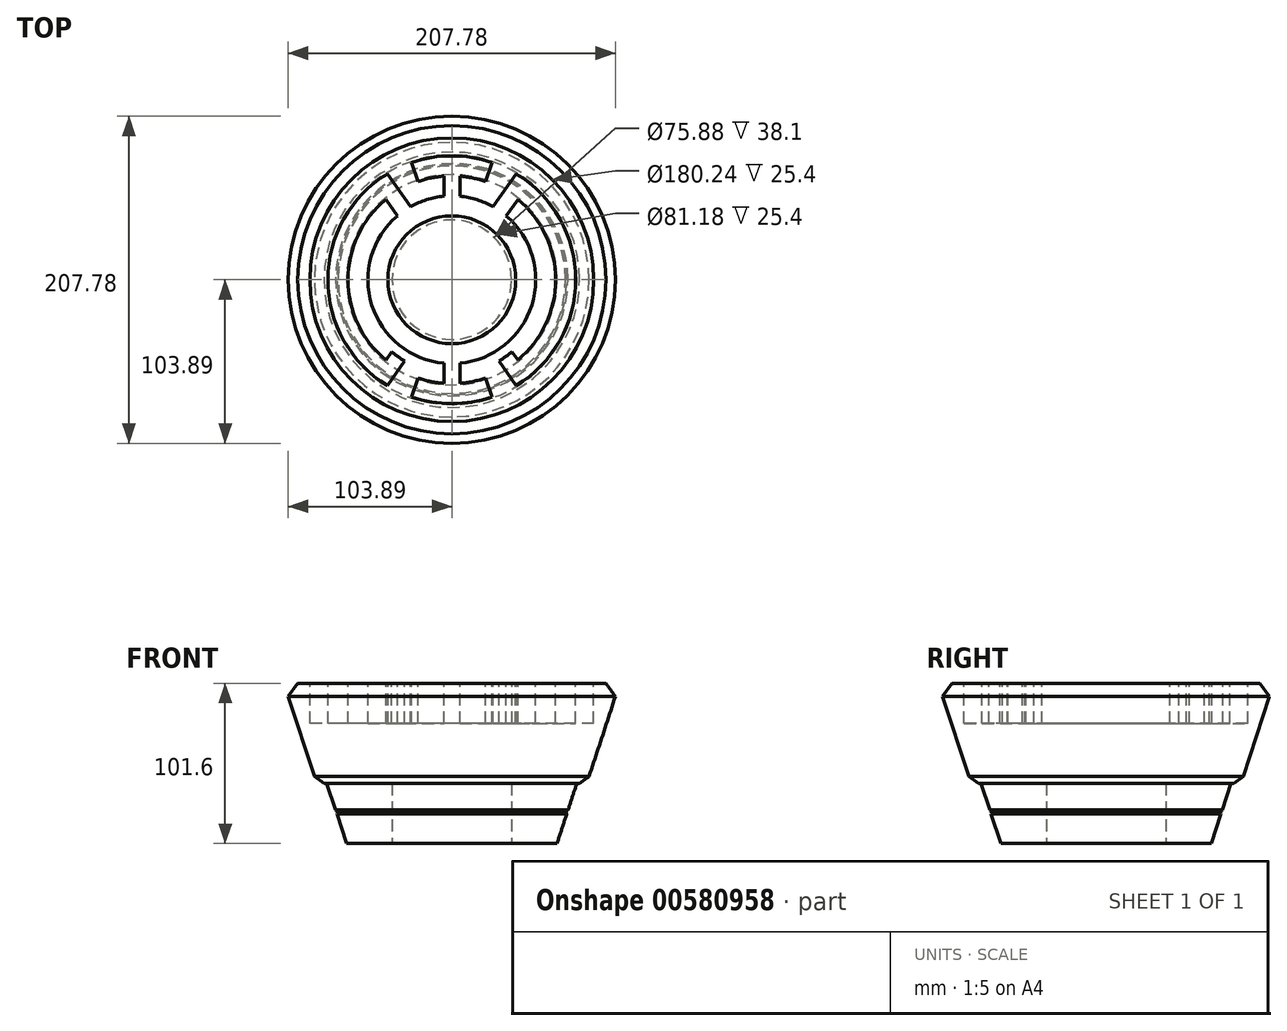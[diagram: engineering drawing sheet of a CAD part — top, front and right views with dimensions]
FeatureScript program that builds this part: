
annotation { "Feature Type Name" : "Feature", "Feature Type Description" : "" }
export const myFeature = defineFeature(function(context is Context, id is Id, definition is map)
    precondition{}
    {
        {
            var Q0;
            Q0=qCreatedBy(makeId("Top.planeOp"),FACE);
            var sketch = newSketch(context, id + "F0", { "sketchPlane" : qUnion([Q0])});
            skCircle(sketch, "E0", {"center": v(0, 0) * mm, "radius": 66.85 * mm});
            skSolve(sketch);
        }
        {
            var Q0;
            Q0=qCreatedBy(makeId("Top.planeOp"),FACE);
            cPlane(context, id + "F1", {"entities" : qUnion([Q0]), "cplaneType" : CPlaneType.OFFSET, "offset" : 101.6 * mm, "width" : 152.4 * mm, "height" : 152.4 * mm});
        }
        {
            var Q0;
            Q0=qCreatedBy(id+"F1.planeOp",FACE);
            var sketch = newSketch(context, id + "F2", { "sketchPlane" : qUnion([Q0])});
            skCircle(sketch, "E1", {"center": v(0, 0) * mm, "radius": 100.28 * mm});
            skSolve(sketch);
        }
        {
            var Q0;
            Q0=makeQuery(id+"F2.imprint","IMPRINT",FACE,{"disambiguationData":[TD([[makeQuery(id+"F2.imprint","IMPRINT",EDGE,{"derivedFrom":sQuery(id+"F2.wireOp",EDGE,"E1")}),1.0]])]});
            var Q1;
            Q1=makeQuery(id+"F0.imprint","IMPRINT",FACE,{"disambiguationData":[TD([[makeQuery(id+"F0.imprint","IMPRINT",EDGE,{"derivedFrom":sQuery(id+"F0.wireOp",EDGE,"E0")}),1.0]])]});
            var Q2;
            Q2=sQuery(id+"F2.wireOp",EDGE,"Eyu8YDiN-lEGU-Wuxt-0ncA-RZLAWeJK4OgB");
            var Q3;
            Q3=sQuery(id+"F0.wireOp",EDGE,"fgfE4CqQ-t5n6-ucAx-yhIW-5wF2yx0Jya2k");
            loft(context, id + "F3", {"sheetProfilesArray" : [{ "sheetProfileEntities" : qUnion([Q0]) }, { "sheetProfileEntities" : qUnion([Q1]) }], "wireProfilesArray" : [{ "wireProfileEntities" : qUnion([Q2]) }, { "wireProfileEntities" : qUnion([Q3]) }]});
        }
        {
            var Q0;
            Q0=qCreatedBy(makeId("Top.planeOp"),FACE);
            var sketch = newSketch(context, id + "F4", { "sketchPlane" : qUnion([Q0])});
            skCircle(sketch, "E2", {"center": v(0, 0) * mm, "radius": 37.94 * mm});
            skSolve(sketch);
        }
        {
            var Q0;
            Q0=makeQuery(id+"F4.imprint","IMPRINT",FACE,{"disambiguationData":[TD([[makeQuery(id+"F4.imprint","IMPRINT",EDGE,{"derivedFrom":sQuery(id+"F4.wireOp",EDGE,"E2")}),1.0]])]});
            extrude(context, id + "F5", {"entities" : qUnion([Q0]), "operationType" : NewBodyOperationType.REMOVE, "depth" : 53.34 * mm, "offsetDistance" : 25.4 * mm});
        }
        {
            var Q0;
            Q0=qCreatedBy(makeId("Top.planeOp"),FACE);
            cPlane(context, id + "F6", {"entities" : qUnion([Q0]), "cplaneType" : CPlaneType.OFFSET, "offset" : 38.1 * mm, "width" : 152.4 * mm, "height" : 152.4 * mm});
        }
        {
            var Q0;
            Q0=qCreatedBy(id+"F6.planeOp",FACE);
            var sketch = newSketch(context, id + "F7", { "sketchPlane" : qUnion([Q0])});
            skCircle(sketch, "E3", {"center": v(0, 0) * mm, "radius": 85.73 * mm});
            skSolve(sketch);
        }
        {
            var Q0;
            Q0=qCreatedBy(id+"F1.planeOp",FACE);
            var sketch = newSketch(context, id + "F8", { "sketchPlane" : qUnion([Q0])});
            skCircle(sketch, "E4", {"center": v(0, 0) * mm, "radius": 106.63 * mm});
            skSolve(sketch);
        }
        {
            var Q1;
            Q1=makeQuery(id+"F7.imprint","IMPRINT",FACE,{"disambiguationData":[TD([[makeQuery(id+"F7.imprint","IMPRINT",EDGE,{"derivedFrom":sQuery(id+"F7.wireOp",EDGE,"E3")}),1.0]])]});
            var Q2;
            Q2=makeQuery(id+"F8.imprint","IMPRINT",FACE,{"disambiguationData":[TD([[makeQuery(id+"F8.imprint","IMPRINT",EDGE,{"derivedFrom":sQuery(id+"F8.wireOp",EDGE,"E4")}),1.0]])]});
            loft(context, id + "F9", {"operationType" : NewBodyOperationType.ADD, "sheetProfilesArray" : [{ "sheetProfileEntities" : qUnion([Q1]) }, { "sheetProfileEntities" : qUnion([Q2]) }]});
        }
        {
            var Q0;
            Q0=makeQuery(id+"F9.opLoft","MID_CAP_EDGE",EDGE,{"disambiguationData":[OSD([sQuery(id+"F7.wireOp",EDGE,"E3")])],"capPos":0.0});
            chamfer(context, id + "F10", {"entities" : qUnion([Q0]), "width" : 6.35 * mm, "tangentPropagation" : true});
        }
        {
            var Q0;
            Q0=makeQuery(id+"F9.opLoft","MID_CAP_EDGE",EDGE,{"disambiguationData":[OSD([sQuery(id+"F7.wireOp",EDGE,"E3"),sQuery(id+"F8.wireOp",EDGE,"E4")])],"capPos":1.0});
            chamfer(context, id + "F11", {"entities" : qUnion([Q0]), "width" : 6.35 * mm, "tangentPropagation" : true});
        }
        {
            var Q0;
            Q0=qCreatedBy(makeId("Front.planeOp"),FACE);
            var sketch = newSketch(context, id + "F12", { "sketchPlane" : qUnion([Q0])});
            skLineSegment(sketch, "E5", {"start": v(-79.4, 38.11) * mm, "end": v(-66.85, 0) * mm});
            skLineSegment(sketch, "E6", {"start": v(-73.8, 21.14) * mm, "end": v(-72.2, 20.33) * mm});
            skLineSegment(sketch, "E7", {"start": v(-72.2, 20.33) * mm, "end": v(-73.02, 18.73) * mm});
            skSolve(sketch);
        }
        {
            var Q0;
            Q0=qCreatedBy(makeId("Right.planeOp"),FACE);
            var sketch = newSketch(context, id + "F13", { "sketchPlane" : qUnion([Q0])});
            skLineSegment(sketch, "E8", {"start": v(0, 0) * mm, "end": v(0, 184.2) * mm});
            skSolve(sketch);
        }
        {
            var Q0;
            Q0=qSketchRegion(id+"F12",true);
            var Q1;
            Q1=sQuery(id+"F13.wireOp",EDGE,"E8");
            revolve(context, id + "F14", {"operationType" : NewBodyOperationType.REMOVE, "entities" : qUnion([Q0]), "axis" : qUnion([Q1]), "revolveType" : RevolveType.FULL, "oppositeDirection" : true});
        }
        {
            var Q0;
            Q0=makeQuery(id+"F9.boolean.opBoolean","MERGE",FACE,{"derivedFrom":[makeQuery(id+"F3.opLoft","CAP_FACE",FACE,{"disambiguationData":[OSD([makeQuery(id+"F2.imprint","IMPRINT",FACE,{"disambiguationData":[TD([[makeQuery(id+"F2.imprint","IMPRINT",EDGE,{"derivedFrom":sQuery(id+"F2.wireOp",EDGE,"E1")}),1.0]])]})])],"isStart":true}),makeQuery(id+"F9.opLoft","CAP_FACE",FACE,{"disambiguationData":[OSD([makeQuery(id+"F8.imprint","IMPRINT",FACE,{"disambiguationData":[TD([[makeQuery(id+"F8.imprint","IMPRINT",EDGE,{"derivedFrom":sQuery(id+"F8.wireOp",EDGE,"E4")}),1.0]])]})])],"isStart":true})]});
            var sketch = newSketch(context, id + "F15", { "sketchPlane" : qUnion([Q0])});
            skCircle(sketch, "E9", {"center": v(0, 0) * mm, "radius": 100.28 * mm});
            skCircle(sketch, "E10.0", {"center": v(0, 0) * mm, "radius": 90.12 * mm});
            skArc(sketch, "E11.0", {"start": v(-34.59, 40.54) * mm, "mid": v(0, -53.29) * mm, "end": v(34.59, 40.54) * mm});
            skCircle(sketch, "E12.0", {"center": v(0, 0) * mm, "radius": 40.59 * mm});
            skArc(sketch, "E13", {"start": v(-33.58, -56.8) * mm, "mid": v(0, -65.99) * mm, "end": v(33.58, -56.8) * mm});
            skCircle(sketch, "E14", {"center": v(0, 0) * mm, "radius": 78.69 * mm});
            skLineSegment(sketch, "E15", {"start": v(-5.08, 53.05) * mm, "end": v(-5.08, 65.8) * mm});
            skLineSegment(sketch, "E16", {"start": v(0, 0) * mm, "end": v(0, 10.8) * mm});
            skLineSegment(sketch, "E17.MirrorCS", {"start": v(21.5, 62.39) * mm, "end": v(25.64, 74.4) * mm});
            skLineSegment(sketch, "E18.MirrorCS", {"start": v(5.08, 53.05) * mm, "end": v(5.08, 65.8) * mm});
            skLineSegment(sketch, "E19.trimOffspring", {"start": v(-21.3, 62.46) * mm, "end": v(-25.64, 74.4) * mm});
            skLineSegment(sketch, "E20", {"start": v(0, 0) * mm, "end": v(13.67, 0) * mm});
            skLineSegment(sketch, "E21.MirrorCS", {"start": v(-5.08, -53.05) * mm, "end": v(-5.08, -65.8) * mm});
            skLineSegment(sketch, "E22.MirrorCS", {"start": v(21.5, -62.39) * mm, "end": v(25.64, -74.4) * mm});
            skLineSegment(sketch, "E23.MirrorCS", {"start": v(-21.3, -62.46) * mm, "end": v(-25.64, -74.4) * mm});
            skLineSegment(sketch, "E24.MirrorCS", {"start": v(5.08, -53.05) * mm, "end": v(5.08, -65.8) * mm});
            skLineSegment(sketch, "E25", {"start": v(-3.74, -3.51) * mm, "end": v(-6.2, 0) * mm});
            skLineSegment(sketch, "E26", {"start": v(4.41, 2.56) * mm, "end": v(0, 8.86) * mm});
            skLineSegment(sketch, "E27.MirrorCS", {"start": v(4.41, -2.56) * mm, "end": v(-26.27, -46.37) * mm});
            skLineSegment(sketch, "E28.MirrorCS", {"start": v(-3.74, 3.51) * mm, "end": v(-34.59, -40.54) * mm});
            skLineSegment(sketch, "E29.trimOffspring", {"start": v(-27.26, 30.07) * mm, "end": v(-41.9, 50.98) * mm});
            skLineSegment(sketch, "E30.trimOffspring", {"start": v(-18.94, 35.9) * mm, "end": v(-40.88, 67.24) * mm});
            skArc(sketch, "E31", {"start": v(-24.79, -54.24) * mm, "mid": v(-33.98, -49.01) * mm, "end": v(-42.1, -42.24) * mm});
            skLineSegment(sketch, "E32.trimOffspring", {"start": v(-38.24, -45.76) * mm, "end": v(-41.9, -50.98) * mm});
            skLineSegment(sketch, "E33.trimOffspring", {"start": v(-29.92, -51.6) * mm, "end": v(-40.88, -67.24) * mm});
            skPoint(sketch, "E34.orphan", {"position": v(-49.2, -61.41) * mm});
            skPoint(sketch, "E35.orphan", {"position": v(-49.2, 61.41) * mm});
            skArc(sketch, "E36.trimOffspring", {"start": v(-41.9, 50.98) * mm, "mid": v(-65.99, 0) * mm, "end": v(-41.9, -50.98) * mm});
            skLineSegment(sketch, "E37.MirrorCS", {"start": v(18.94, 35.9) * mm, "end": v(40.88, 67.24) * mm});
            skLineSegment(sketch, "E38.MirrorCS", {"start": v(27.26, 30.07) * mm, "end": v(41.9, 50.98) * mm});
            skLineSegment(sketch, "E39.MirrorCS", {"start": v(38.24, -45.76) * mm, "end": v(41.9, -50.98) * mm});
            skArc(sketch, "E40.MirrorCS", {"start": v(24.79, -54.24) * mm, "mid": v(33.98, -49.01) * mm, "end": v(42.1, -42.24) * mm});
            skLineSegment(sketch, "E41.MirrorCS", {"start": v(29.92, -51.6) * mm, "end": v(40.88, -67.24) * mm});
            skArc(sketch, "E42.trimOffspring", {"start": v(41.9, -50.98) * mm, "mid": v(65.99, 0) * mm, "end": v(41.9, 50.98) * mm});
            skArc(sketch, "E43.trimOffspring", {"start": v(33.58, 56.8) * mm, "mid": v(0, 65.99) * mm, "end": v(-33.58, 56.8) * mm});
            skArc(sketch, "E44.trimOffspring", {"start": v(26.27, 46.37) * mm, "mid": v(0, 53.29) * mm, "end": v(-26.27, 46.37) * mm});
            skSolve(sketch);
        }
        {
            var Q0;
            {var subQ6=sQuery(id+"F15.wireOp",EDGE,"E21.MirrorCS");Q0=makeQuery(id+"F15.imprint","IMPRINT",FACE,{"disambiguationData":[TD([[makeQuery(id+"F15.imprint","IMPRINT",EDGE,{"derivedFrom":subQ6}),-1.0]])]});}
            var Q1;
            {var subQ0=sQuery(id+"F15.wireOp",EDGE,"E12.0");var subQ4=makeQuery(id+"F15.imprint","INTERSECT",VERTEX,{"derivedFrom":[subQ0,sQuery(id+"F15.wireOp",EDGE,"E37.MirrorCS")]});Q1=makeQuery(id+"F15.imprint","IMPRINT",FACE,{"disambiguationData":[TD([[makeQuery(id+"F15.imprint","IMPRINT",EDGE,{"disambiguationData":[TD([[subQ4,1.0]])],"derivedFrom":subQ0}),1.0]])]});}
            var Q2;
            {var subQ0=sQuery(id+"F15.wireOp",EDGE,"E24.MirrorCS");Q2=makeQuery(id+"F15.imprint","IMPRINT",FACE,{"disambiguationData":[TD([[makeQuery(id+"F15.imprint","IMPRINT",EDGE,{"derivedFrom":subQ0}),1.0]])]});}
            var Q3;
            {var subQ3=sQuery(id+"F15.wireOp",EDGE,"E23.MirrorCS");Q3=makeQuery(id+"F15.imprint","IMPRINT",FACE,{"disambiguationData":[TD([[makeQuery(id+"F15.imprint","IMPRINT",EDGE,{"derivedFrom":subQ3}),-1.0]])]});}
            var Q4;
            Q4=makeQuery(id+"F15.imprint","IMPRINT",FACE,{"disambiguationData":[TD([[makeQuery(id+"F15.imprint","IMPRINT",EDGE,{"derivedFrom":sQuery(id+"F15.wireOp",EDGE,"E10.0")}),1.0]])]});
            var Q5;
            {var subQ3=sQuery(id+"F15.wireOp",EDGE,"E22.MirrorCS");Q5=makeQuery(id+"F15.imprint","IMPRINT",FACE,{"disambiguationData":[TD([[makeQuery(id+"F15.imprint","IMPRINT",EDGE,{"derivedFrom":subQ3}),1.0]])]});}
            var Q6;
            {var subQ4=sQuery(id+"F15.wireOp",EDGE,"E15");Q6=makeQuery(id+"F15.imprint","IMPRINT",FACE,{"disambiguationData":[TD([[makeQuery(id+"F15.imprint","IMPRINT",EDGE,{"derivedFrom":subQ4}),1.0]])]});}
            var Q7;
            {var subQ4=sQuery(id+"F15.wireOp",EDGE,"E18.MirrorCS");Q7=makeQuery(id+"F15.imprint","IMPRINT",FACE,{"disambiguationData":[TD([[makeQuery(id+"F15.imprint","IMPRINT",EDGE,{"derivedFrom":subQ4}),-1.0]])]});}
            var Q8;
            {var subQ0=sQuery(id+"F15.wireOp",EDGE,"E17.MirrorCS");Q8=makeQuery(id+"F15.imprint","IMPRINT",FACE,{"disambiguationData":[TD([[makeQuery(id+"F15.imprint","IMPRINT",EDGE,{"derivedFrom":subQ0}),-1.0]])]});}
            var Q9;
            {var subQ0=sQuery(id+"F15.wireOp",EDGE,"E19.trimOffspring");Q9=makeQuery(id+"F15.imprint","IMPRINT",FACE,{"disambiguationData":[TD([[makeQuery(id+"F15.imprint","IMPRINT",EDGE,{"derivedFrom":subQ0}),1.0]])]});}
            extrude(context, id + "F16", {"entities" : qUnion([Q0, Q1, Q2, Q3, Q4, Q5, Q6, Q7, Q8, Q9]), "operationType" : NewBodyOperationType.REMOVE, "oppositeDirection" : true, "depth" : 25.4 * mm, "offsetDistance" : 25.4 * mm});
        }
    });
